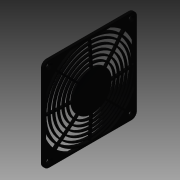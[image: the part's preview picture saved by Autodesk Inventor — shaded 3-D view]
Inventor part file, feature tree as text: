
AUTODESK INVENTOR PART (.ipt)
format: ipt  version: 2016 SP1 (Build 200210100, 210)  size: 888,832 bytes
history: native  units: mm
features: sketch x5, extrude x4, other x4, projected_geometry x3, plane x2, revolve x2, pattern_circular x2, fillet x2, hole x1
ambient origin geometry x8: Origin, YZ Plane, XZ Plane, XY Plane, X Axis, Y Axis, Z Axis, Center Point
bodies: Solid1 (feature_tree)
feature tree (25):
  extrude  "Extrusion1"  Depth=119.0mm
  sketch  "Sketch2"  dims[d2=3.8mm d3=0.0mm d4=105.0mm]
  plane  "Work Plane2"
  sketch  "Sketch3"  dims[d5=52.5mm d6=105.0mm]
  revolve  "Revolution2"  [1 undecoded]
  revolve  "Revolution3"  [1 undecoded]
  hole  "Hole2"  [1 undecoded]
  plane  "Work Plane3"
  sketch  "Sketch6"  dims[d9=59.5mm d67=3.5mm d68=3.5mm d69=119.0mm d70=59.5mm d72=1.0mm d74=90.0deg d75=90.0deg d76=4.5mm d77=6.0mm d78=8.0mm d79=2.0mm d80=90.0deg d81=8.0mm d82=20.594885mm d139=50.0mm d140=4.0mm d141=1.5mm d142=4.0mm d143=1.5mm d144=4.0mm d145=1.5mm d146=4.0mm d147=1.5mm d148=4.0mm d149=1.5mm d155=2.0mm d156=1.0mm d157=3.8mm d158=0.0mm d160=4.0mm d173=40.0mm d175=360.0deg d180=56.5mm d181=40.0mm d183=360.0deg d190=10.0mm d191=0.0mm d192=40.0mm d193=360.0deg d196=7.0mm d198=2.0mm d199=1.0mm d211=10.0mm d212=0.0mm d213=80.0mm d214=360.0deg d216=0.5mm]
  extrude  "Extrusion3"  Depth=0.5mm
  extrude  "Extrusion4"  Depth=0.5mm
  other  "Work Axis1"
  pattern_circular  "Circular Pattern1"  [2 undecoded]
  fillet  "Fillet1"  Radius=59.5mm
  extrude  "Extrusion5"  Depth=0.5mm
  other  "Work Axis2"
  pattern_circular  "Circular Pattern2"  Angle=90.0deg  [1 undecoded]
  fillet  "Fillet2"  [1 undecoded]
  sketch  "Sketch1"  dims[d0=119.0mm d1=119.0mm]
  projected_geometry  "Projected Loop1"
  projected_geometry  "Projected Loop2"
  other  "Image1"
  sketch  "Sketch4"  dims[d7=52.5mm d8=119.0mm]
  other  "Image2"
  projected_geometry  "Projected Loop3"
note: 7 required parameter values undecoded (feature->parameter linkage not recoverable at this tier; creation-order binding heuristic only, values carry confidence <= 0.55)